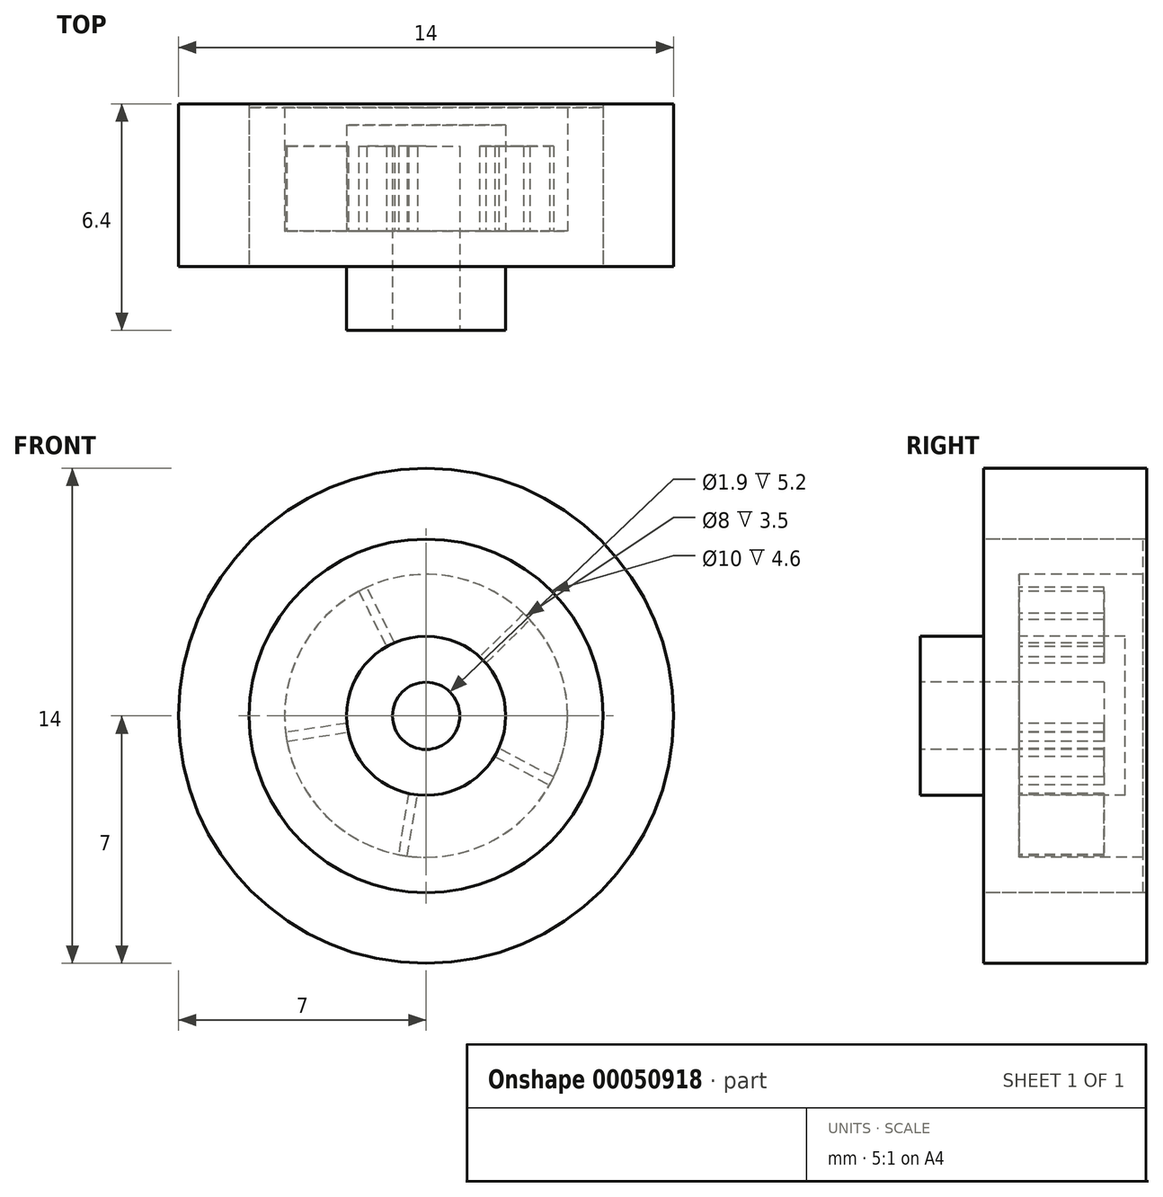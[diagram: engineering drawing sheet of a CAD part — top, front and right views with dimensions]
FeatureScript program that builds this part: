
annotation { "Feature Type Name" : "Feature", "Feature Type Description" : "" }
export const myFeature = defineFeature(function(context is Context, id is Id, definition is map)
    precondition{}
    {
        {
            var Q0;
            Q0=qCreatedBy(makeId("Front.planeOp"),FACE);
            var sketch = newSketch(context, id + "F0", { "sketchPlane" : qUnion([Q0])});
            skCircle(sketch, "E0", {"center": v(0, 0) * mm, "radius": 7 * mm});
            skCircle(sketch, "E1", {"center": v(0, 0) * mm, "radius": 5 * mm});
            skCircle(sketch, "E2", {"center": v(0, 0) * mm, "radius": 2.25 * mm});
            skCircle(sketch, "E3", {"center": v(0, 0) * mm, "radius": 0.95 * mm});
            skCircle(sketch, "E4", {"center": v(0, 0) * mm, "radius": 4 * mm});
            skSolve(sketch);
        }
        {
            var Q0;
            Q0=makeQuery(id+"F0.imprint","IMPRINT",FACE,{"disambiguationData":[TD([[makeQuery(id+"F0.imprint","IMPRINT",EDGE,{"derivedFrom":sQuery(id+"F0.wireOp",EDGE,"E0")}),1.0]])]});
            extrude(context, id + "F1", {"entities" : qUnion([Q0]), "oppositeDirection" : true, "depth" : 4.6 * mm});
        }
        {
            var Q0;
            Q0=makeQuery(id+"F0.imprint","IMPRINT",FACE,{"disambiguationData":[TD([[makeQuery(id+"F0.imprint","IMPRINT",EDGE,{"derivedFrom":sQuery(id+"F0.wireOp",EDGE,"E1")}),1.0]])]});
            extrude(context, id + "F2", {"entities" : qUnion([Q0]), "oppositeDirection" : true, "depth" : 4.5 * mm});
        }
        {
            var Q0;
            Q0=makeQuery(id+"F0.imprint","IMPRINT",FACE,{"disambiguationData":[TD([[makeQuery(id+"F0.imprint","IMPRINT",EDGE,{"derivedFrom":sQuery(id+"F0.wireOp",EDGE,"E2")}),-1.0]])]});
            extrude(context, id + "F3", {"entities" : qUnion([Q0]), "operationType" : NewBodyOperationType.ADD, "oppositeDirection" : true, "depth" : 1 * mm});
        }
        {
            var Q0;
            Q0=makeQuery(id+"F0.imprint","IMPRINT",FACE,{"disambiguationData":[TD([[makeQuery(id+"F0.imprint","IMPRINT",EDGE,{"derivedFrom":sQuery(id+"F0.wireOp",EDGE,"E2")}),1.0]])]});
            extrude(context, id + "F4", {"entities" : qUnion([Q0]), "operationType" : NewBodyOperationType.ADD, "oppositeDirection" : true, "depth" : 4 * mm, "hasSecondDirection" : true, "secondDirectionOppositeDirection" : false, "secondDirectionDepth" : 1.8 * mm});
        }
        {
            var Q0;
            Q0=makeQuery(id+"F3.opExtrude","CAP_FACE",FACE,{"disambiguationData":[OSD([sQuery(id+"F0.wireOp",EDGE,"E2"),sQuery(id+"F0.wireOp",EDGE,"E4")])],"isStart":false});
            var sketch = newSketch(context, id + "F5", { "sketchPlane" : qUnion([Q0])});
            skCircle(sketch, "E5.cCircle", {"center": v(0, 0) * mm, "radius": 2.25 * mm, "construction": true});
            skLineSegment(sketch, "E5.0", {"start": v(1, 2.01) * mm, "end": v(2.22, -0.33) * mm, "construction": true});
            skLineSegment(sketch, "E5.1", {"start": v(2.22, -0.33) * mm, "end": v(0.37, -2.22) * mm, "construction": true});
            skLineSegment(sketch, "E5.2", {"start": v(0.37, -2.22) * mm, "end": v(-2, -1.04) * mm, "construction": true});
            skLineSegment(sketch, "E5.3", {"start": v(-2, -1.04) * mm, "end": v(-1.6, 1.58) * mm, "construction": true});
            skLineSegment(sketch, "E5.4", {"start": v(-1.6, 1.58) * mm, "end": v(1, 2.01) * mm, "construction": true});
            skLineSegment(sketch, "E6", {"start": v(-1.6, 1.58) * mm, "end": v(-3.01, 2.97) * mm, "construction": true});
            skPoint(sketch, "E7", {"position": v(-2.3, 2.27) * mm});
            skPoint(sketch, "E8", {"position": v(1.48, 2.75) * mm});
            skPoint(sketch, "E9", {"position": v(3.09, -0.48) * mm});
            skPoint(sketch, "E10", {"position": v(0.6, -3.07) * mm});
            skPoint(sketch, "E11", {"position": v(-2.81, -1.36) * mm});
            skLineSegment(sketch, "E12", {"start": v(-2.93, 3.06) * mm, "end": v(-1.4, 1.57) * mm});
            skLineSegment(sketch, "E13", {"start": v(-1.5, 1.68) * mm, "end": v(-1.7, 1.47) * mm});
            skLineSegment(sketch, "E14", {"start": v(-1.59, 1.39) * mm, "end": v(-3.1, 2.88) * mm});
            skLineSegment(sketch, "E15", {"start": v(-3.1, 2.88) * mm, "end": v(-2.93, 3.06) * mm});
            skLineSegment(sketch, "E16", {"start": v(-1.4, 1.57) * mm, "end": v(-1.59, 1.39) * mm});
            skLineSegment(sketch, "E17.1.0", {"start": v(-3.81, -1.84) * mm, "end": v(-1.93, -0.86) * mm});
            skLineSegment(sketch, "E17.1.1", {"start": v(-1.8, -1.08) * mm, "end": v(-3.7, -2.06) * mm});
            skLineSegment(sketch, "E17.1.2", {"start": v(-3.7, -2.06) * mm, "end": v(-3.81, -1.84) * mm});
            skLineSegment(sketch, "E17.2.0", {"start": v(0.57, -4.2) * mm, "end": v(0.22, -2.1) * mm});
            skLineSegment(sketch, "E17.2.1", {"start": v(0.47, -2.05) * mm, "end": v(0.82, -4.15) * mm});
            skLineSegment(sketch, "E17.2.2", {"start": v(0.82, -4.15) * mm, "end": v(0.57, -4.2) * mm});
            skLineSegment(sketch, "E18.1.3.0", {"start": v(4.16, -0.76) * mm, "end": v(2.06, -0.44) * mm});
            skLineSegment(sketch, "E18.3.3.0", {"start": v(2.1, -0.19) * mm, "end": v(4.2, -0.5) * mm});
            skLineSegment(sketch, "E18.6.3.0", {"start": v(4.2, -0.5) * mm, "end": v(4.16, -0.76) * mm});
            skLineSegment(sketch, "E18.1.4.0", {"start": v(2, 3.73) * mm, "end": v(1.05, 1.82) * mm});
            skLineSegment(sketch, "E18.3.4.0", {"start": v(0.83, 1.94) * mm, "end": v(1.78, 3.84) * mm});
            skLineSegment(sketch, "E18.6.4.0", {"start": v(1.78, 3.84) * mm, "end": v(2, 3.73) * mm});
            skCircle(sketch, "E19.0", {"center": v(0, 0) * mm, "radius": 0.95 * mm});
            skLineSegment(sketch, "E20", {"start": v(0.83, 1.94) * mm, "end": v(1.05, 1.82) * mm});
            skLineSegment(sketch, "E21", {"start": v(-1.93, -0.86) * mm, "end": v(-1.8, -1.08) * mm});
            skLineSegment(sketch, "E22", {"start": v(0.22, -2.1) * mm, "end": v(0.47, -2.05) * mm});
            skLineSegment(sketch, "E23", {"start": v(2.1, -0.19) * mm, "end": v(2.06, -0.44) * mm});
            skSolve(sketch);
        }
        {
            var Q0;
            {var subQ0=sQuery(id+"F5.wireOp",EDGE,"E18.1.4.0");var subQ1=makeQuery(id+"F3.opExtrude","CAP_EDGE",EDGE,{"disambiguationData":[OSD([sQuery(id+"F0.wireOp",EDGE,"E4")])],"isStart":false});var subQ2=makeQuery(id+"F5.imprint","INTERSECT",VERTEX,{"derivedFrom":[subQ1,subQ0]});Q0=makeQuery(id+"F5.imprint","IMPRINT",FACE,{"disambiguationData":[TD([[makeQuery(id+"F5.imprint","IMPRINT",EDGE,{"disambiguationData":[TD([[subQ2,-1.0]])],"derivedFrom":subQ0}),-1.0]])]});}
            var Q1;
            {var subQ0=sQuery(id+"F5.wireOp",EDGE,"E18.6.4.0");Q1=makeQuery(id+"F5.imprint","IMPRINT",FACE,{"disambiguationData":[TD([[makeQuery(id+"F5.imprint","IMPRINT",EDGE,{"derivedFrom":subQ0}),-1.0]])]});}
            var Q2;
            {var subQ0=sQuery(id+"F5.wireOp",EDGE,"E18.1.3.0");var subQ1=makeQuery(id+"F3.opExtrude","CAP_EDGE",EDGE,{"disambiguationData":[OSD([sQuery(id+"F0.wireOp",EDGE,"E4")])],"isStart":false});var subQ2=makeQuery(id+"F5.imprint","INTERSECT",VERTEX,{"derivedFrom":[subQ1,subQ0]});Q2=makeQuery(id+"F5.imprint","IMPRINT",FACE,{"disambiguationData":[TD([[makeQuery(id+"F5.imprint","IMPRINT",EDGE,{"disambiguationData":[TD([[subQ2,-1.0]])],"derivedFrom":subQ0}),-1.0]])]});}
            var Q3;
            {var subQ0=sQuery(id+"F5.wireOp",EDGE,"E18.6.3.0");Q3=makeQuery(id+"F5.imprint","IMPRINT",FACE,{"disambiguationData":[TD([[makeQuery(id+"F5.imprint","IMPRINT",EDGE,{"derivedFrom":subQ0}),-1.0]])]});}
            var Q4;
            {var subQ0=sQuery(id+"F5.wireOp",EDGE,"E23");Q4=makeQuery(id+"F5.imprint","IMPRINT",FACE,{"disambiguationData":[TD([[makeQuery(id+"F5.imprint","IMPRINT",EDGE,{"derivedFrom":subQ0}),1.0]])]});}
            var Q5;
            {var subQ0=sQuery(id+"F5.wireOp",EDGE,"E20");Q5=makeQuery(id+"F5.imprint","IMPRINT",FACE,{"disambiguationData":[TD([[makeQuery(id+"F5.imprint","IMPRINT",EDGE,{"derivedFrom":subQ0}),1.0]])]});}
            var Q6;
            {var subQ0=sQuery(id+"F5.wireOp",EDGE,"E17.2.0");var subQ1=makeQuery(id+"F3.opExtrude","CAP_EDGE",EDGE,{"disambiguationData":[OSD([sQuery(id+"F0.wireOp",EDGE,"E4")])],"isStart":false});var subQ2=makeQuery(id+"F5.imprint","INTERSECT",VERTEX,{"derivedFrom":[subQ1,subQ0]});Q6=makeQuery(id+"F5.imprint","IMPRINT",FACE,{"disambiguationData":[TD([[makeQuery(id+"F5.imprint","IMPRINT",EDGE,{"disambiguationData":[TD([[subQ2,-1.0]])],"derivedFrom":subQ0}),-1.0]])]});}
            var Q7;
            {var subQ0=sQuery(id+"F5.wireOp",EDGE,"E17.2.2");Q7=makeQuery(id+"F5.imprint","IMPRINT",FACE,{"disambiguationData":[TD([[makeQuery(id+"F5.imprint","IMPRINT",EDGE,{"derivedFrom":subQ0}),-1.0]])]});}
            var Q8;
            {var subQ0=sQuery(id+"F5.wireOp",EDGE,"E22");Q8=makeQuery(id+"F5.imprint","IMPRINT",FACE,{"disambiguationData":[TD([[makeQuery(id+"F5.imprint","IMPRINT",EDGE,{"derivedFrom":subQ0}),-1.0]])]});}
            var Q9;
            {var subQ0=sQuery(id+"F5.wireOp",EDGE,"E16");Q9=makeQuery(id+"F5.imprint","IMPRINT",FACE,{"disambiguationData":[TD([[makeQuery(id+"F5.imprint","IMPRINT",EDGE,{"derivedFrom":subQ0}),-1.0]])]});}
            var Q10;
            {var subQ0=sQuery(id+"F5.wireOp",EDGE,"E12");var subQ1=makeQuery(id+"F3.opExtrude","CAP_EDGE",EDGE,{"disambiguationData":[OSD([sQuery(id+"F0.wireOp",EDGE,"E4")])],"isStart":false});var subQ2=makeQuery(id+"F5.imprint","INTERSECT",VERTEX,{"derivedFrom":[subQ1,subQ0]});Q10=makeQuery(id+"F5.imprint","IMPRINT",FACE,{"disambiguationData":[TD([[makeQuery(id+"F5.imprint","IMPRINT",EDGE,{"disambiguationData":[TD([[subQ2,-1.0]])],"derivedFrom":subQ0}),-1.0]])]});}
            var Q11;
            {var subQ0=sQuery(id+"F5.wireOp",EDGE,"E21");Q11=makeQuery(id+"F5.imprint","IMPRINT",FACE,{"disambiguationData":[TD([[makeQuery(id+"F5.imprint","IMPRINT",EDGE,{"derivedFrom":subQ0}),-1.0]])]});}
            var Q12;
            {var subQ0=sQuery(id+"F5.wireOp",EDGE,"E17.1.0");var subQ1=makeQuery(id+"F3.opExtrude","CAP_EDGE",EDGE,{"disambiguationData":[OSD([sQuery(id+"F0.wireOp",EDGE,"E4")])],"isStart":false});var subQ2=makeQuery(id+"F5.imprint","INTERSECT",VERTEX,{"derivedFrom":[subQ1,subQ0]});Q12=makeQuery(id+"F5.imprint","IMPRINT",FACE,{"disambiguationData":[TD([[makeQuery(id+"F5.imprint","IMPRINT",EDGE,{"disambiguationData":[TD([[subQ2,-1.0]])],"derivedFrom":subQ0}),-1.0]])]});}
            extrude(context, id + "F6", {"entities" : qUnion([Q0, Q1, Q2, Q3, Q4, Q5, Q6, Q7, Q8, Q9, Q10, Q11, Q12]), "operationType" : NewBodyOperationType.ADD, "depth" : 2.4 * mm});
        }
        {
            var Q0;
            Q0=makeQuery(id+"F5.imprint","IMPRINT",FACE,{"disambiguationData":[TD([[makeQuery(id+"F5.imprint","IMPRINT",EDGE,{"derivedFrom":sQuery(id+"F5.wireOp",EDGE,"E19.0")}),-1.0]])]});
            extrude(context, id + "F7", {"entities" : qUnion([Q0]), "operationType" : NewBodyOperationType.ADD, "oppositeDirection" : true, "depth" : 1 * mm});
        }
        {
            var Q0;
            Q0=makeQuery(id+"F4.opExtrude","CAP_FACE",FACE,{"disambiguationData":[OSD([sQuery(id+"F0.wireOp",EDGE,"E2"),sQuery(id+"F0.wireOp",EDGE,"E3")])],"isStart":false});
            var sketch = newSketch(context, id + "F8", { "sketchPlane" : qUnion([Q0])});
            skCircle(sketch, "E24.0", {"center": v(0, 0) * mm, "radius": 0.95 * mm});
            skSolve(sketch);
        }
        {
            var Q0;
            Q0=makeQuery(id+"F8.imprint","IMPRINT",FACE,{"disambiguationData":[TD([[makeQuery(id+"F8.imprint","IMPRINT",EDGE,{"derivedFrom":sQuery(id+"F8.wireOp",EDGE,"E24.0")}),-1.0]])]});
            extrude(context, id + "F9", {"entities" : qUnion([Q0]), "operationType" : NewBodyOperationType.ADD, "oppositeDirection" : true, "depth" : 0.6 * mm});
        }
    });
